# Revit family: WCBrushHolder-Vitra-QLineSeries-A44999
name_source: partatom
category: Plumbing Fixtures
revit_build: Autodesk Revit 2017 (Build: 20160225_1515(x64)
units: mm (PartAtom-declared; Revit-internal decimal feet)

## family parameters
Cut with Voids When Loaded = No
Host = Face
OmniClass Number = 23.45.00.00
OmniClass Title = Sanitary, Laundry, and Cleaning Equipment
Part Type = Normal
Room Calculation Point = No
Round Connector Dimension = Use Diameter
Shared = Yes

## types (1)
- WCBrushHolder-Vitra-QLineSeries-A44999
    Article No. (default) = A44999
    BIMobject category = Accessories
    Brand = VitrA
    CW Connection = No
    Coating Material = Glass
    Color = Chrome
    Default Elevation = 0 mm  [stored 0 ft]
    Description = Q Line WC Brush Holder
    Design country = Turkey
    HW Connection = No
    IFC Classification = Sanitary Terminal
    Manufacturer = Vitra
    Manufacturer name = Vitra
    Masterformat 2014 Code = 10 28 13
    Masterformat 2014 Description = Toilet Accessories
    Model = A44999
    Mounting type = Wall Mounted
    NBS Referans Code = 35-75-86
    NBS Referans Description = Toilet Brush Holders
    Nominal Depth (mm) = 140 mm  [stored 0.459318 ft]
    Nominal Height (mm) = 360 mm  [stored 1.1811 ft]
    Nominal Width (mm) = 110 mm  [stored 0.360892 ft]
    OmniClass Code = 23-31 25 00
    OmniClass Description = Toilet and Bath Specialties
    Product SKU = A44999
    Product Type = WC Brush Holder
    Product certification = https://www.vitraglobal.com
    Product family = Q Line
    Product group = Q Line WC Brush Holder
    Product url = https://www.vitra.com.tr
    Secondary Material = Chrome (Metal)
    Technical description = https://www.vitra.com.tr
    UNSPSC Description = Plumbing Fixtures
    URL = https://vitraglobal.com
    Uniclass 1.4 Code = L7313
    Uniclass 1.4 Description = Sanitary above ground pipes and fittings
    Uniclass 2.0 Code = PR-35-75-86
    Uniclass 2.0 Description = Toilet Brush Holders
    Uniclass 2015 Code = PR_40_20_76_86
    Uniclass 2015 Name = Toilet Brush Holders
    Uniformat II Code = D2010
    Uniformat II Description = Plumbing Fixtures
    Vent Connection = No
    Warranty Period (Year) = 5 Years
    Waste Connection = No
    Weight Net (kg) = 3
    Youtube = https://www.youtube.com

note: [stored X ft] marks values corroborated as IEEE doubles in the binary element streams (Revit-internal decimal feet)

## geometry (parser evidence)
native form markers: Sweep x3
no freeform markers — native parametric forms only
